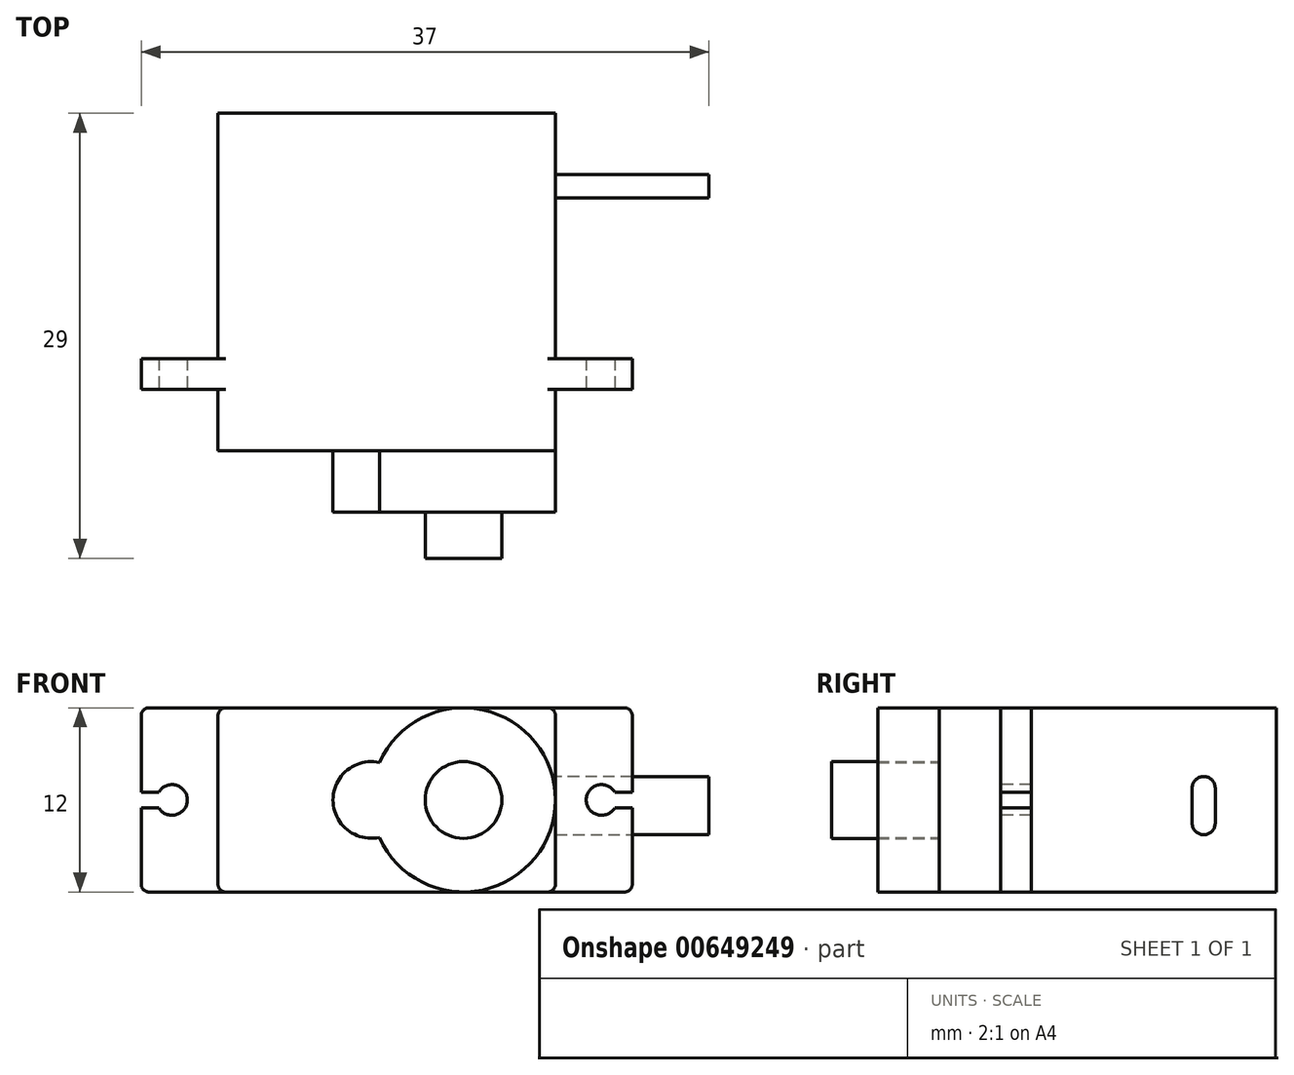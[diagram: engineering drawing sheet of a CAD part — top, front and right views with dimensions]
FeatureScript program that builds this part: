
annotation { "Feature Type Name" : "Feature", "Feature Type Description" : "" }
export const myFeature = defineFeature(function(context is Context, id is Id, definition is map)
    precondition{}
    {
        {
            var Q0;
            Q0=qCreatedBy(makeId("Top.planeOp"),FACE);
            var sketch = newSketch(context, id + "F0", { "sketchPlane" : qUnion([Q0])});
            skLineSegment(sketch, "E0.bottom", {"start": v(11, -11) * mm, "end": v(-11, -11) * mm});
            skLineSegment(sketch, "E0.top", {"start": v(11, 11) * mm, "end": v(-11, 11) * mm});
            skLineSegment(sketch, "E0.left", {"start": v(11, -11) * mm, "end": v(11, 11) * mm});
            skLineSegment(sketch, "E0.right", {"start": v(-11, -11) * mm, "end": v(-11, 11) * mm});
            skPoint(sketch, "E0.middle", {"position": v(0, 0) * mm});
            skLineSegment(sketch, "E1.bottom", {"start": v(-11, -7) * mm, "end": v(-16, -7) * mm});
            skLineSegment(sketch, "E1.top", {"start": v(-11, -5) * mm, "end": v(-16, -5) * mm});
            skLineSegment(sketch, "E1.left", {"start": v(-11, -7) * mm, "end": v(-11, -5) * mm});
            skLineSegment(sketch, "E1.right", {"start": v(-16, -7) * mm, "end": v(-16, -5) * mm});
            skLineSegment(sketch, "E2.bottom", {"start": v(11, -5) * mm, "end": v(16, -5) * mm});
            skLineSegment(sketch, "E2.top", {"start": v(11, -7) * mm, "end": v(16, -7) * mm});
            skLineSegment(sketch, "E2.left", {"start": v(11, -5) * mm, "end": v(11, -7) * mm});
            skLineSegment(sketch, "E2.right", {"start": v(16, -5) * mm, "end": v(16, -7) * mm});
            skSolve(sketch);
        }
        {
            var Q0;
            Q0=qSketchRegion(id+"F0",true);
            extrude(context, id + "F1", {"entities" : qUnion([Q0]), "depth" : 12 * mm});
        }
        {
            var Q0;
            {var subQ0=sQuery(id+"F0.wireOp",EDGE,"E0.left");Q0=makeQuery(id+"F1.opExtrude","CAP_EDGE",EDGE,{"disambiguationData":[OSD([subQ0]),TDD([makeQuery(id+"F0.imprint","IMPRINT",EDGE,{"disambiguationData":[TD([[makeQuery(id+"F0.imprint","INTERSECT",VERTEX,{"derivedFrom":[sQuery(id+"F0.wireOp",EDGE,"E0.top"),subQ0]}),1.0]])],"derivedFrom":subQ0})])],"isStart":false});}
            var Q1;
            {var subQ0=sQuery(id+"F0.wireOp",EDGE,"E0.left");Q1=makeQuery(id+"F1.opExtrude","CAP_EDGE",EDGE,{"disambiguationData":[OSD([subQ0]),TDD([makeQuery(id+"F0.imprint","IMPRINT",EDGE,{"disambiguationData":[TD([[makeQuery(id+"F0.imprint","INTERSECT",VERTEX,{"derivedFrom":[sQuery(id+"F0.wireOp",EDGE,"E0.bottom"),subQ0]}),-1.0]])],"derivedFrom":subQ0})])],"isStart":false});}
            var Q2;
            {var subQ0=sQuery(id+"F0.wireOp",EDGE,"E0.right");Q2=makeQuery(id+"F1.opExtrude","CAP_EDGE",EDGE,{"disambiguationData":[OSD([subQ0]),TDD([makeQuery(id+"F0.imprint","IMPRINT",EDGE,{"disambiguationData":[TD([[makeQuery(id+"F0.imprint","INTERSECT",VERTEX,{"derivedFrom":[sQuery(id+"F0.wireOp",EDGE,"E0.bottom"),subQ0]}),-1.0]])],"derivedFrom":subQ0})])],"isStart":false});}
            var Q3;
            Q3=makeQuery(id+"F1.opExtrude","CAP_EDGE",EDGE,{"disambiguationData":[OSD([sQuery(id+"F0.wireOp",EDGE,"E2.right")])],"isStart":false});
            var Q4;
            {var subQ0=sQuery(id+"F0.wireOp",EDGE,"E0.right");Q4=makeQuery(id+"F1.opExtrude","CAP_EDGE",EDGE,{"disambiguationData":[OSD([subQ0]),TDD([makeQuery(id+"F0.imprint","IMPRINT",EDGE,{"disambiguationData":[TD([[makeQuery(id+"F0.imprint","INTERSECT",VERTEX,{"derivedFrom":[sQuery(id+"F0.wireOp",EDGE,"E0.top"),subQ0]}),1.0]])],"derivedFrom":subQ0})])],"isStart":false});}
            var Q5;
            Q5=makeQuery(id+"F1.opExtrude","CAP_EDGE",EDGE,{"disambiguationData":[OSD([sQuery(id+"F0.wireOp",EDGE,"E1.right")])],"isStart":false});
            var Q6;
            {var subQ0=sQuery(id+"F0.wireOp",EDGE,"E0.right");Q6=makeQuery(id+"F1.opExtrude","CAP_EDGE",EDGE,{"disambiguationData":[OSD([subQ0]),TDD([makeQuery(id+"F0.imprint","IMPRINT",EDGE,{"disambiguationData":[TD([[makeQuery(id+"F0.imprint","INTERSECT",VERTEX,{"derivedFrom":[sQuery(id+"F0.wireOp",EDGE,"E0.top"),subQ0]}),1.0]])],"derivedFrom":subQ0})])],"isStart":true});}
            var Q7;
            {var subQ0=sQuery(id+"F0.wireOp",EDGE,"E0.right");Q7=makeQuery(id+"F1.opExtrude","CAP_EDGE",EDGE,{"disambiguationData":[OSD([subQ0]),TDD([makeQuery(id+"F0.imprint","IMPRINT",EDGE,{"disambiguationData":[TD([[makeQuery(id+"F0.imprint","INTERSECT",VERTEX,{"derivedFrom":[sQuery(id+"F0.wireOp",EDGE,"E0.bottom"),subQ0]}),-1.0]])],"derivedFrom":subQ0})])],"isStart":true});}
            var Q8;
            Q8=makeQuery(id+"F1.opExtrude","CAP_EDGE",EDGE,{"disambiguationData":[OSD([sQuery(id+"F0.wireOp",EDGE,"E1.right")])],"isStart":true});
            var Q9;
            {var subQ0=sQuery(id+"F0.wireOp",EDGE,"E0.left");Q9=makeQuery(id+"F1.opExtrude","CAP_EDGE",EDGE,{"disambiguationData":[OSD([subQ0]),TDD([makeQuery(id+"F0.imprint","IMPRINT",EDGE,{"disambiguationData":[TD([[makeQuery(id+"F0.imprint","INTERSECT",VERTEX,{"derivedFrom":[sQuery(id+"F0.wireOp",EDGE,"E0.bottom"),subQ0]}),-1.0]])],"derivedFrom":subQ0})])],"isStart":true});}
            var Q10;
            {var subQ0=sQuery(id+"F0.wireOp",EDGE,"E0.left");Q10=makeQuery(id+"F1.opExtrude","CAP_EDGE",EDGE,{"disambiguationData":[OSD([subQ0]),TDD([makeQuery(id+"F0.imprint","IMPRINT",EDGE,{"disambiguationData":[TD([[makeQuery(id+"F0.imprint","INTERSECT",VERTEX,{"derivedFrom":[sQuery(id+"F0.wireOp",EDGE,"E0.top"),subQ0]}),1.0]])],"derivedFrom":subQ0})])],"isStart":true});}
            var Q11;
            Q11=makeQuery(id+"F1.opExtrude","CAP_EDGE",EDGE,{"disambiguationData":[OSD([sQuery(id+"F0.wireOp",EDGE,"E2.right")])],"isStart":true});
            fillet(context, id + "F2", {"entities" : qUnion([Q0, Q1, Q2, Q3, Q4, Q5, Q6, Q7, Q8, Q9, Q10, Q11]), "radius" : 0.5 * mm, "tangentPropagation" : true, "allowEdgeOverflow" : false});
        }
        {
            var Q0;
            Q0=makeQuery(id+"F1.opExtrude","SWEPT_FACE",FACE,{"disambiguationData":[OSD([sQuery(id+"F0.wireOp",EDGE,"E0.bottom")])]});
            var sketch = newSketch(context, id + "F3", { "sketchPlane" : qUnion([Q0])});
            skCircle(sketch, "E3", {"center": v(5, 6) * mm, "radius": 6 * mm});
            skCircle(sketch, "E4", {"center": v(-1, 6) * mm, "radius": 2.5 * mm});
            skSolve(sketch);
        }
        {
            var Q0;
            Q0=qSketchRegion(id+"F3",true);
            extrude(context, id + "F4", {"entities" : qUnion([Q0]), "operationType" : NewBodyOperationType.ADD, "depth" : 4 * mm});
        }
        {
            var Q0;
            Q0=makeQuery(id+"F4.opExtrude","CAP_FACE",FACE,{"disambiguationData":[OSD([sQuery(id+"F3.wireOp",EDGE,"E3"),sQuery(id+"F3.wireOp",EDGE,"E4")])],"isStart":false});
            var sketch = newSketch(context, id + "F5", { "sketchPlane" : qUnion([Q0])});
            skCircle(sketch, "E5", {"center": v(5, 6) * mm, "radius": 2.5 * mm});
            skSolve(sketch);
        }
        {
            var Q0;
            Q0=makeQuery(id+"F5.imprint","IMPRINT",FACE,{"disambiguationData":[TD([[makeQuery(id+"F5.imprint","IMPRINT",EDGE,{"derivedFrom":sQuery(id+"F5.wireOp",EDGE,"E5")}),1.0]])]});
            extrude(context, id + "F6", {"entities" : qUnion([Q0]), "depth" : 3 * mm});
        }
        {
            var Q0;
            {var subQ0=sQuery(id+"F0.wireOp",EDGE,"E0.left");Q0=makeQuery(id+"F1.opExtrude","SWEPT_FACE",FACE,{"disambiguationData":[OSD([subQ0]),TDD([makeQuery(id+"F0.imprint","IMPRINT",EDGE,{"disambiguationData":[TD([[makeQuery(id+"F0.imprint","INTERSECT",VERTEX,{"derivedFrom":[sQuery(id+"F0.wireOp",EDGE,"E0.top"),subQ0]}),1.0]])],"derivedFrom":subQ0})])]});}
            var sketch = newSketch(context, id + "F7", { "sketchPlane" : qUnion([Q0])});
            skLineSegment(sketch, "E6.bottom", {"start": v(5.5, 3.73) * mm, "end": v(7, 3.73) * mm});
            skLineSegment(sketch, "E6.top", {"start": v(5.5, 7.53) * mm, "end": v(7, 7.53) * mm});
            skLineSegment(sketch, "E6.left", {"start": v(5.5, 3.73) * mm, "end": v(5.5, 7.53) * mm});
            skLineSegment(sketch, "E6.right", {"start": v(7, 3.73) * mm, "end": v(7, 7.53) * mm});
            skSolve(sketch);
        }
        {
            var Q0;
            Q0=makeQuery(id+"F7.imprint","IMPRINT",FACE,{"disambiguationData":[TD([[makeQuery(id+"F7.imprint","IMPRINT",EDGE,{"derivedFrom":sQuery(id+"F7.wireOp",EDGE,"E6.bottom")}),1.0]])]});
            extrude(context, id + "F8", {"entities" : qUnion([Q0]), "depth" : 10 * mm});
        }
        {
            var Q0;
            Q0=makeQuery(id+"F8.opExtrude","SWEPT_EDGE",EDGE,{"disambiguationData":[OSD([sQuery(id+"F7.wireOp",EDGE,"E6.top"),sQuery(id+"F7.wireOp",EDGE,"E6.left")])]});
            var Q1;
            Q1=makeQuery(id+"F8.opExtrude","SWEPT_EDGE",EDGE,{"disambiguationData":[OSD([sQuery(id+"F7.wireOp",EDGE,"E6.top"),sQuery(id+"F7.wireOp",EDGE,"E6.right")])]});
            var Q2;
            Q2=makeQuery(id+"F8.opExtrude","SWEPT_EDGE",EDGE,{"disambiguationData":[OSD([sQuery(id+"F7.wireOp",EDGE,"E6.bottom"),sQuery(id+"F7.wireOp",EDGE,"E6.left")])]});
            var Q3;
            Q3=makeQuery(id+"F8.opExtrude","SWEPT_EDGE",EDGE,{"disambiguationData":[OSD([sQuery(id+"F7.wireOp",EDGE,"E6.bottom"),sQuery(id+"F7.wireOp",EDGE,"E6.right")])]});
            fillet(context, id + "F9", {"entities" : qUnion([Q0, Q1, Q2, Q3]), "radius" : 0.75 * mm, "tangentPropagation" : true, "allowEdgeOverflow" : false});
        }
        {
            var Q0;
            Q0=makeQuery(id+"F1.opExtrude","SWEPT_FACE",FACE,{"disambiguationData":[OSD([sQuery(id+"F0.wireOp",EDGE,"E2.top")])]});
            var sketch = newSketch(context, id + "F10", { "sketchPlane" : qUnion([Q0])});
            skCircle(sketch, "E7", {"center": v(14, 6) * mm, "radius": 1 * mm});
            skPoint(sketch, "E7.centerSnap0", {"position": v(16, 6) * mm});
            skLineSegment(sketch, "E8.bottom", {"start": v(16, 6.5) * mm, "end": v(14, 6.5) * mm});
            skLineSegment(sketch, "E8.top", {"start": v(16, 5.5) * mm, "end": v(14, 5.5) * mm});
            skLineSegment(sketch, "E8.left", {"start": v(16, 6.5) * mm, "end": v(16, 5.5) * mm});
            skLineSegment(sketch, "E8.right", {"start": v(14, 6.5) * mm, "end": v(14, 5.5) * mm});
            skLineSegment(sketch, "E9", {"start": v(0, 12.23) * mm, "end": v(0, 0) * mm, "construction": true});
            skLineSegment(sketch, "E10.MirrorCS", {"start": v(-14, 6.5) * mm, "end": v(-14, 5.5) * mm});
            skLineSegment(sketch, "E11.MirrorCS", {"start": v(-16, 6.5) * mm, "end": v(-16, 5.5) * mm});
            skLineSegment(sketch, "E12.MirrorCS", {"start": v(-16, 6.5) * mm, "end": v(-14, 6.5) * mm});
            skLineSegment(sketch, "E13.MirrorCS", {"start": v(-16, 5.5) * mm, "end": v(-14, 5.5) * mm});
            skCircle(sketch, "E14.MirrorC", {"center": v(-14, 6) * mm, "radius": 1 * mm});
            skPoint(sketch, "E15.MirrorP", {"position": v(-16, 6) * mm});
            skSolve(sketch);
        }
        {
            var Q0;
            {var subQ5=sQuery(id+"F10.wireOp",EDGE,"E8.right");Q0=makeQuery(id+"F10.imprint","IMPRINT",FACE,{"disambiguationData":[TD([[makeQuery(id+"F10.imprint","IMPRINT",EDGE,{"derivedFrom":subQ5}),1.0]])]});}
            var Q1;
            {var subQ5=sQuery(id+"F10.wireOp",EDGE,"E8.right");Q1=makeQuery(id+"F10.imprint","IMPRINT",FACE,{"disambiguationData":[TD([[makeQuery(id+"F10.imprint","IMPRINT",EDGE,{"derivedFrom":subQ5}),-1.0]])]});}
            var Q2;
            {var subQ5=sQuery(id+"F10.wireOp",EDGE,"E8.left");Q2=makeQuery(id+"F10.imprint","IMPRINT",FACE,{"disambiguationData":[TD([[makeQuery(id+"F10.imprint","IMPRINT",EDGE,{"derivedFrom":subQ5}),-1.0]])]});}
            var Q3;
            {var subQ0=sQuery(id+"F10.wireOp",EDGE,"E10.MirrorCS");Q3=makeQuery(id+"F10.imprint","IMPRINT",FACE,{"disambiguationData":[TD([[makeQuery(id+"F10.imprint","IMPRINT",EDGE,{"derivedFrom":subQ0}),1.0]])]});}
            var Q4;
            {var subQ0=sQuery(id+"F10.wireOp",EDGE,"E11.MirrorCS");Q4=makeQuery(id+"F10.imprint","IMPRINT",FACE,{"disambiguationData":[TD([[makeQuery(id+"F10.imprint","IMPRINT",EDGE,{"derivedFrom":subQ0}),1.0]])]});}
            var Q5;
            {var subQ0=sQuery(id+"F10.wireOp",EDGE,"E10.MirrorCS");Q5=makeQuery(id+"F10.imprint","IMPRINT",FACE,{"disambiguationData":[TD([[makeQuery(id+"F10.imprint","IMPRINT",EDGE,{"derivedFrom":subQ0}),-1.0]])]});}
            var Q6;
            Q6=makeQuery(id+"F1.opExtrude","SWEPT_FACE",FACE,{"disambiguationData":[OSD([sQuery(id+"F0.wireOp",EDGE,"E2.bottom")])]});
            extrude(context, id + "F11", {"entities" : qUnion([Q0, Q1, Q2, Q3, Q4, Q5]), "operationType" : NewBodyOperationType.REMOVE, "endBound" : BoundingType.UP_TO_SURFACE, "oppositeDirection" : true, "endBoundEntityFace" : qUnion([Q6]), "depth" : 25 * mm});
        }
    });
